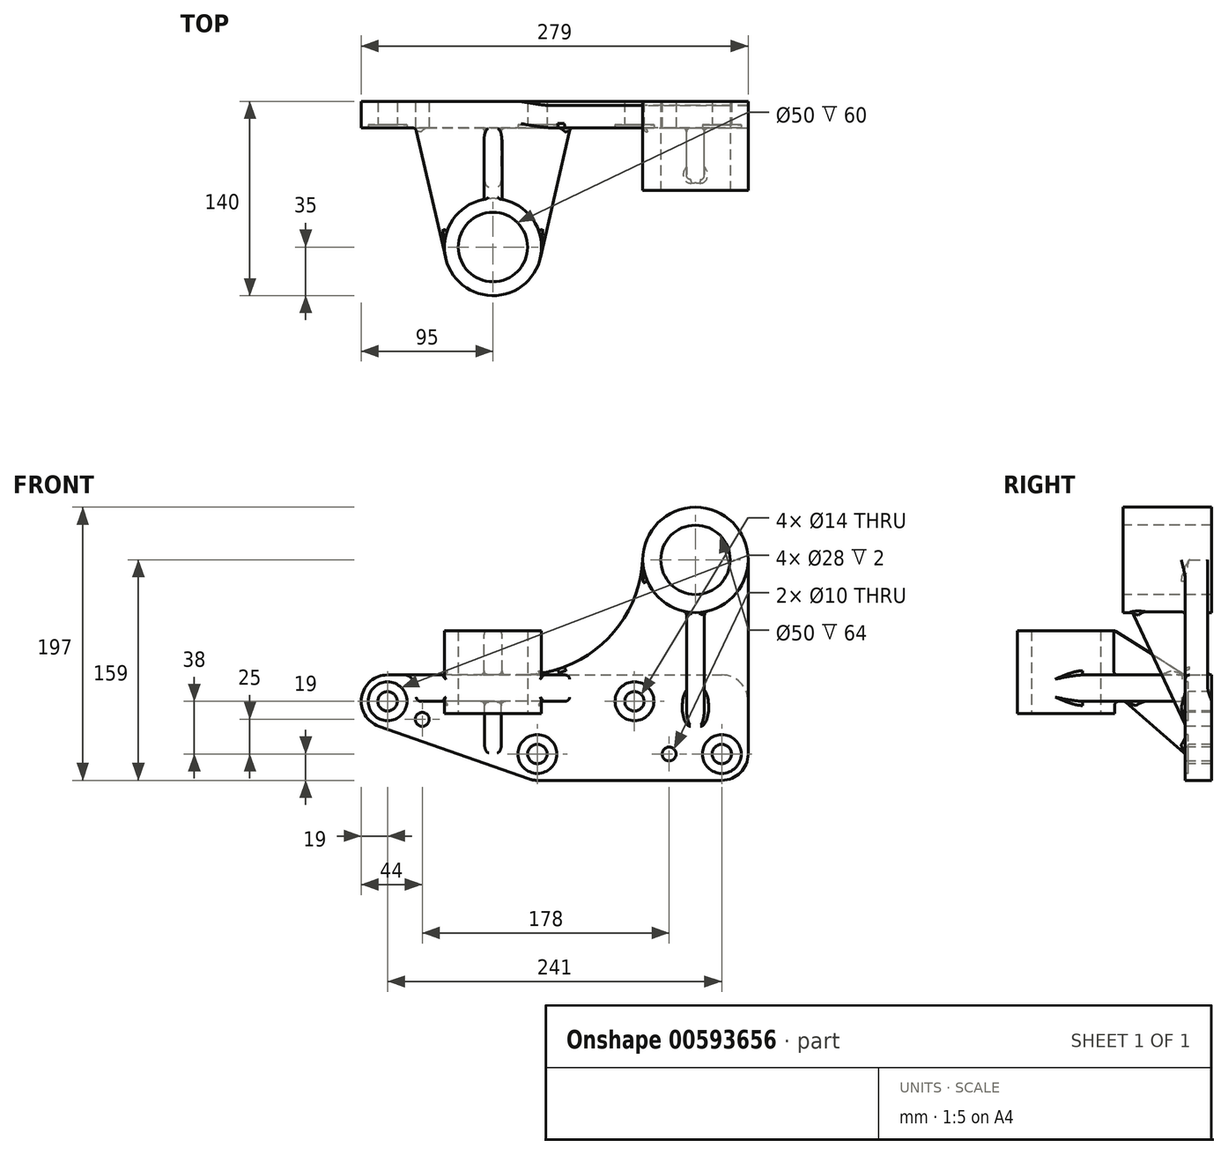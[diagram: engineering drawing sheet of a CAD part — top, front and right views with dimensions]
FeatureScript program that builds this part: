
annotation { "Feature Type Name" : "Feature", "Feature Type Description" : "" }
export const myFeature = defineFeature(function(context is Context, id is Id, definition is map)
    precondition{}
    {
        {
            var Q0;
            Q0=qCreatedBy(makeId("Front.planeOp"),FACE);
            var sketch = newSketch(context, id + "F0", { "sketchPlane" : qUnion([Q0])});
            skArc(sketch, "E0", {"start": v(0, -19) * mm, "mid": v(13.44, -13.44) * mm, "end": v(19, 0) * mm});
            skLineSegment(sketch, "E1", {"start": v(0, -19) * mm, "end": v(-133, -19) * mm});
            skLineSegment(sketch, "E2", {"start": v(-57.06, 140) * mm, "end": v(-57, 140) * mm, "construction": true});
            skArc(sketch, "E3", {"start": v(19, 140) * mm, "mid": v(-19, 178) * mm, "end": v(-57, 140) * mm});
            skLineSegment(sketch, "E4", {"start": v(19, 0) * mm, "end": v(19, 140) * mm});
            skLineSegment(sketch, "E5", {"start": v(-241, 57) * mm, "end": v(-144.86, 57) * mm});
            skArc(sketch, "E6", {"start": v(-241, 57) * mm, "mid": v(-259.73, 41.2) * mm, "end": v(-247.3, 20.08) * mm});
            skPoint(sketch, "E7", {"position": v(-133, 0) * mm});
            skLineSegment(sketch, "E8", {"start": v(-133, -19) * mm, "end": v(-133, 0) * mm, "construction": true});
            skArc(sketch, "E9", {"start": v(-139.3, -17.92) * mm, "mid": v(-136.2, -18.73) * mm, "end": v(-133, -19) * mm});
            skLineSegment(sketch, "E10", {"start": v(-247.3, 20.08) * mm, "end": v(-139.3, -17.92) * mm});
            skArc(sketch, "E11", {"start": v(-144.86, 57) * mm, "mid": v(-84.43, 81.03) * mm, "end": v(-57, 140) * mm});
            skSolve(sketch);
        }
        {
            var Q0;
            Q0 = qSketchRegion(id + "F0", true);
            extrude(context, id + "F1", {"entities" : qUnion([Q0]), "depth" : 19 * mm, "offsetDistance" : 25 * mm});
        }
        {
            var Q0;
            Q0=makeQuery(id+"F1.opExtrude","CAP_FACE",FACE,{"disambiguationData":[OSD([sQuery(id+"F0.wireOp",EDGE,"E0"),sQuery(id+"F0.wireOp",EDGE,"E1"),sQuery(id+"F0.wireOp",EDGE,"E3"),sQuery(id+"F0.wireOp",EDGE,"E4"),sQuery(id+"F0.wireOp",EDGE,"E5"),sQuery(id+"F0.wireOp",EDGE,"E6"),sQuery(id+"F0.wireOp",EDGE,"E9"),sQuery(id+"F0.wireOp",EDGE,"E10"),sQuery(id+"F0.wireOp",EDGE,"E11")])],"isStart":true});
            var sketch = newSketch(context, id + "F2", { "sketchPlane" : qUnion([Q0])});
            skCircle(sketch, "E12", {"center": v(19, 140) * mm, "radius": 38 * mm});
            skSolve(sketch);
        }
        {
            var Q0;
            Q0 = qSketchRegion(id + "F2", true);
            extrude(context, id + "F3", {"entities" : qUnion([Q0]), "operationType" : NewBodyOperationType.ADD, "oppositeDirection" : true, "depth" : 64 * mm, "offsetDistance" : 25 * mm});
        }
        {
            var Q0;
            Q0=makeQuery(id+"F1.opExtrude","SWEPT_FACE",FACE,{"disambiguationData":[OSD([sQuery(id+"F0.wireOp",EDGE,"E5")])]});
            var sketch = newSketch(context, id + "F4", { "sketchPlane" : qUnion([Q0])});
            skLineSegment(sketch, "E13", {"start": v(19, -64) * mm, "end": v(-57, -64) * mm});
            skPoint(sketch, "E14", {"position": v(-19, -64) * mm});
            skLineSegment(sketch, "E15", {"start": v(-165, -19) * mm, "end": v(-165, -105) * mm, "construction": true});
            skArc(sketch, "E16", {"start": v(-199.1, -112.87) * mm, "mid": v(-165, -140) * mm, "end": v(-130.9, -112.87) * mm});
            skLineSegment(sketch, "E17", {"start": v(-130.9, -112.87) * mm, "end": v(-109.22, -19) * mm});
            skLineSegment(sketch, "E18.MirrorCS", {"start": v(-199.1, -112.87) * mm, "end": v(-220.78, -19) * mm});
            skLineSegment(sketch, "E19", {"start": v(-109.22, -19) * mm, "end": v(-220.78, -19) * mm});
            skSolve(sketch);
        }
        {
            var Q0;
            Q0 = qSketchRegion(id + "F4", true);
            extrude(context, id + "F5", {"entities" : qUnion([Q0]), "operationType" : NewBodyOperationType.ADD, "oppositeDirection" : true, "depth" : 19 * mm, "offsetDistance" : 25 * mm});
        }
        {
            var Q0;
            Q0=makeQuery(id+"F5.boolean.opBoolean","MERGE",FACE,{"derivedFrom":[makeQuery(id+"F1.opExtrude","SWEPT_FACE",FACE,{"disambiguationData":[OSD([sQuery(id+"F0.wireOp",EDGE,"E5")])]}),makeQuery(id+"F5.opExtrude","CAP_FACE",FACE,{"disambiguationData":[OSD([sQuery(id+"F4.wireOp",EDGE,"E16"),sQuery(id+"F4.wireOp",EDGE,"E17"),sQuery(id+"F4.wireOp",EDGE,"E18.MirrorCS"),sQuery(id+"F4.wireOp",EDGE,"E19")])],"isStart":true})]});
            var sketch = newSketch(context, id + "F6", { "sketchPlane" : qUnion([Q0])});
            skCircle(sketch, "E20", {"center": v(-165, -105) * mm, "radius": 35 * mm});
            skSolve(sketch);
        }
        {
            var Q0;
            Q0 = qSketchRegion(id + "F6", true);
            extrude(context, id + "F7", {"entities" : qUnion([Q0]), "operationType" : NewBodyOperationType.ADD, "depth" : 32 * mm, "offsetDistance" : 25 * mm, "hasSecondDirection" : true, "secondDirectionOppositeDirection" : true, "secondDirectionDepth" : 28 * mm});
        }
        {
            var Q0;
            Q0=makeQuery(id+"F1.opExtrude","CAP_FACE",FACE,{"disambiguationData":[OSD([sQuery(id+"F0.wireOp",EDGE,"E0"),sQuery(id+"F0.wireOp",EDGE,"E1"),sQuery(id+"F0.wireOp",EDGE,"E3"),sQuery(id+"F0.wireOp",EDGE,"E4"),sQuery(id+"F0.wireOp",EDGE,"E5"),sQuery(id+"F0.wireOp",EDGE,"E6"),sQuery(id+"F0.wireOp",EDGE,"E9"),sQuery(id+"F0.wireOp",EDGE,"E10"),sQuery(id+"F0.wireOp",EDGE,"E11")])],"isStart":true});
            var sketch = newSketch(context, id + "F8", { "sketchPlane" : qUnion([Q0])});
            skLineSegment(sketch, "E21", {"start": v(-19, 38) * mm, "end": v(-19, 140) * mm});
            skArc(sketch, "E22.0", {"start": v(144.86, 57) * mm, "mid": v(84.43, 81.03) * mm, "end": v(57, 140) * mm});
            skArc(sketch, "E23", {"start": v(-19, 140) * mm, "mid": v(19, 102) * mm, "end": v(57, 140) * mm});
            skLineSegment(sketch, "E24", {"start": v(144.86, 57) * mm, "end": v(0, 57) * mm});
            skArc(sketch, "E25", {"start": v(0, 57) * mm, "mid": v(-13.44, 51.44) * mm, "end": v(-19, 38) * mm});
            skSolve(sketch);
        }
        {
            var Q0;
            Q0 = qSketchRegion(id + "F8", true);
            extrude(context, id + "F9", {"entities" : qUnion([Q0]), "operationType" : NewBodyOperationType.REMOVE, "oppositeDirection" : true, "depth" : 3 * mm, "offsetDistance" : 25 * mm});
        }
        {
            var Q0;
            Q0=makeQuery(id+"F9.boolean.opBoolean","MERGE",FACE,{"derivedFrom":[makeQuery(id+"F3.boolean.opBoolean","MERGE",FACE,{"derivedFrom":[makeQuery(id+"F1.opExtrude","SWEPT_FACE",FACE,{"disambiguationData":[OSD([sQuery(id+"F0.wireOp",EDGE,"E3")])]}),makeQuery(id+"F3.opExtrude","SWEPT_FACE",FACE,{"disambiguationData":[OSD([sQuery(id+"F2.wireOp",EDGE,"E12")])]})]}),makeQuery(id+"F9.opExtrude","SWEPT_FACE",FACE,{"disambiguationData":[OSD([sQuery(id+"F8.wireOp",EDGE,"E23")])]})]});
            cPlane(context, id + "F10", {"entities" : qUnion([Q0]), "cplaneType" : CPlaneType.LINE_ANGLE, "offset" : 25 * mm, "angle" : 90 * degree, "oppositeDirection" : true, "width" : 150 * mm, "height" : 150 * mm});
        }
        {
            var Q0;
            Q0=qCreatedBy(id+"F10.planeOp",FACE);
            var sketch = newSketch(context, id + "F11", { "sketchPlane" : qUnion([Q0])});
            skLineSegment(sketch, "E26.0", {"start": v(64, 178) * mm, "end": v(64, 102) * mm, "construction": true});
            skLineSegment(sketch, "E27.0", {"start": v(0, 178) * mm, "end": v(0, 102) * mm, "construction": true});
            skLineSegment(sketch, "E28", {"start": v(64, 178) * mm, "end": v(0, 178) * mm, "construction": true});
            skLineSegment(sketch, "E29", {"start": v(64, 102) * mm, "end": v(0, 102) * mm, "construction": true});
            skLineSegment(sketch, "E30", {"start": v(59.33, 107) * mm, "end": v(19, 107) * mm});
            skPoint(sketch, "E31", {"position": v(57, 102) * mm});
            skLineSegment(sketch, "E32", {"start": v(57, 102) * mm, "end": v(19, 20.5) * mm});
            skLineSegment(sketch, "E33", {"start": v(19, 20.5) * mm, "end": v(19, 107) * mm});
            skLineSegment(sketch, "E34", {"start": v(57, 102) * mm, "end": v(59.33, 107) * mm});
            skSolve(sketch);
        }
        {
            var Q0;
            Q0=makeQuery(id+"F11.imprint","IMPRINT",FACE,{"disambiguationData":[TD([[makeQuery(id+"F11.imprint","IMPRINT",EDGE,{"derivedFrom":sQuery(id+"F11.wireOp",EDGE,"E30")}),1.0]])]});
            extrude(context, id + "F12", {"entities" : qUnion([Q0]), "operationType" : NewBodyOperationType.ADD, "endBound" : BoundingType.SYMMETRIC, "depth" : 13 * mm, "offsetDistance" : 25 * mm});
        }
        {
            var Q0;
            Q0=makeQuery(id+"F7.boolean.opBoolean","MERGE",FACE,{"derivedFrom":[makeQuery(id+"F5.opExtrude","SWEPT_FACE",FACE,{"disambiguationData":[OSD([sQuery(id+"F4.wireOp",EDGE,"E16")])]}),makeQuery(id+"F7.opExtrude","SWEPT_FACE",FACE,{"disambiguationData":[OSD([sQuery(id+"F6.wireOp",EDGE,"E20")])]})]});
            cPlane(context, id + "F13", {"entities" : qUnion([Q0]), "cplaneType" : CPlaneType.LINE_ANGLE, "offset" : 25 * mm, "angle" : 0 * degree, "width" : 150 * mm, "height" : 150 * mm});
        }
        {
            var Q0;
            Q0=qCreatedBy(id+"F13.planeOp",FACE);
            var sketch = newSketch(context, id + "F14", { "sketchPlane" : qUnion([Q0])});
            skLineSegment(sketch, "E35.0", {"start": v(-140, 89) * mm, "end": v(-70, 89) * mm, "construction": true});
            skLineSegment(sketch, "E36.0", {"start": v(-140, 29) * mm, "end": v(-70, 29) * mm, "construction": true});
            skLineSegment(sketch, "E37", {"start": v(-70, 89) * mm, "end": v(-70, 29) * mm, "construction": true});
            skLineSegment(sketch, "E38", {"start": v(-75, 89) * mm, "end": v(-75, 57) * mm});
            skLineSegment(sketch, "E39", {"start": v(-75, 89) * mm, "end": v(-70, 89) * mm});
            skLineSegment(sketch, "E40", {"start": v(-70, 89) * mm, "end": v(-19, 57) * mm});
            skLineSegment(sketch, "E41", {"start": v(-19, 57) * mm, "end": v(-75, 57) * mm});
            skSolve(sketch);
        }
        {
            var Q0;
            Q0=makeQuery(id+"F14.imprint","IMPRINT",FACE,{"disambiguationData":[TD([[makeQuery(id+"F14.imprint","IMPRINT",EDGE,{"derivedFrom":sQuery(id+"F14.wireOp",EDGE,"E38")}),1.0]])]});
            extrude(context, id + "F15", {"entities" : qUnion([Q0]), "operationType" : NewBodyOperationType.ADD, "endBound" : BoundingType.SYMMETRIC, "depth" : 13 * mm, "offsetDistance" : 25 * mm});
        }
        {
            var Q0;
            Q0=qCreatedBy(id+"F13.planeOp",FACE);
            var sketch = newSketch(context, id + "F16", { "sketchPlane" : qUnion([Q0])});
            skLineSegment(sketch, "E42", {"start": v(-19, 0) * mm, "end": v(-19, 43) * mm});
            skLineSegment(sketch, "E43", {"start": v(-19, 43) * mm, "end": v(-68.47, 43) * mm});
            skLineSegment(sketch, "E44", {"start": v(-19, 0) * mm, "end": v(-68.47, 43) * mm});
            skSolve(sketch);
        }
        {
            var Q0;
            Q0=makeQuery(id+"F16.imprint","IMPRINT",FACE,{"disambiguationData":[TD([[makeQuery(id+"F16.imprint","IMPRINT",EDGE,{"derivedFrom":sQuery(id+"F16.wireOp",EDGE,"E42")}),1.0]])]});
            extrude(context, id + "F17", {"entities" : qUnion([Q0]), "operationType" : NewBodyOperationType.ADD, "endBound" : BoundingType.SYMMETRIC, "depth" : 12 * mm, "offsetDistance" : 25 * mm});
        }
        {
            var Q0;
            Q0=makeQuery(id+"F1.opExtrude","CAP_FACE",FACE,{"disambiguationData":[OSD([sQuery(id+"F0.wireOp",EDGE,"E0"),sQuery(id+"F0.wireOp",EDGE,"E1"),sQuery(id+"F0.wireOp",EDGE,"E3"),sQuery(id+"F0.wireOp",EDGE,"E4"),sQuery(id+"F0.wireOp",EDGE,"E5"),sQuery(id+"F0.wireOp",EDGE,"E6"),sQuery(id+"F0.wireOp",EDGE,"E9"),sQuery(id+"F0.wireOp",EDGE,"E10"),sQuery(id+"F0.wireOp",EDGE,"E11")])],"isStart":false});
            var sketch = newSketch(context, id + "F18", { "sketchPlane" : qUnion([Q0])});
            skPoint(sketch, "E45", {"position": v(-241, 38) * mm});
            skPoint(sketch, "E46", {"position": v(-216, 25) * mm});
            skPoint(sketch, "E47", {"position": v(-133, 0) * mm});
            skPoint(sketch, "E48", {"position": v(-38, 0) * mm});
            skPoint(sketch, "E49", {"position": v(-63, 38) * mm});
            skPoint(sketch, "E50", {"position": v(0, 0) * mm});
            skSolve(sketch);
        }
        {
            var Q0;
            Q0=makeQuery(id+"F7.opExtrude","CAP_FACE",FACE,{"disambiguationData":[OSD([sQuery(id+"F6.wireOp",EDGE,"E20")])],"isStart":true});
            var sketch = newSketch(context, id + "F19", { "sketchPlane" : qUnion([Q0])});
            skPoint(sketch, "E51", {"position": v(-165, 105) * mm});
            skSolve(sketch);
        }
        {
            var Q0;
            Q0=makeQuery(id+"F3.opExtrude","CAP_FACE",FACE,{"disambiguationData":[OSD([sQuery(id+"F2.wireOp",EDGE,"E12")])],"isStart":false});
            var sketch = newSketch(context, id + "F20", { "sketchPlane" : qUnion([Q0])});
            skPoint(sketch, "E52", {"position": v(-19, 140) * mm});
            skSolve(sketch);
        }
        {
            var Q0;
            Q0=sQuery(id+"F18.wireOp",VERTEX,"E46");
            var Q1;
            Q1=sQuery(id+"F18.wireOp",VERTEX,"E48");
            var Q2;
            Q2=makeQuery(id+"F1.opExtrude","SWEPT_BODY",BODY,{"disambiguationData":[OSD([sQuery(id+"F0.wireOp",EDGE,"E0"),sQuery(id+"F0.wireOp",EDGE,"E1"),sQuery(id+"F0.wireOp",EDGE,"E3"),sQuery(id+"F0.wireOp",EDGE,"E4"),sQuery(id+"F0.wireOp",EDGE,"E5"),sQuery(id+"F0.wireOp",EDGE,"E6"),sQuery(id+"F0.wireOp",EDGE,"E9"),sQuery(id+"F0.wireOp",EDGE,"E10"),sQuery(id+"F0.wireOp",EDGE,"E11")])]});
            hole(context, id + "F21", {"style" : HoleStyle.SIMPLE, "endStyle" : HoleEndStyle.THROUGH, "holeDiameter" : 10 * mm, "majorDiameter" : 6.35 * mm, "tappedDepth" : 12 * mm, "tapClearance" : 3, "startFromSketch" : true, "locations" : qUnion([Q0, Q1]), "scope" : qUnion([Q2])});
        }
        {
            var Q0;
            Q0=sQuery(id+"F18.wireOp",VERTEX,"E45");
            var Q1;
            Q1=sQuery(id+"F18.wireOp",VERTEX,"E47");
            var Q2;
            Q2=sQuery(id+"F18.wireOp",VERTEX,"E49");
            var Q3;
            Q3=sQuery(id+"F18.wireOp",VERTEX,"E50");
            var Q4;
            Q4=makeQuery(id+"F1.opExtrude","SWEPT_BODY",BODY,{"disambiguationData":[OSD([sQuery(id+"F0.wireOp",EDGE,"E0"),sQuery(id+"F0.wireOp",EDGE,"E1"),sQuery(id+"F0.wireOp",EDGE,"E3"),sQuery(id+"F0.wireOp",EDGE,"E4"),sQuery(id+"F0.wireOp",EDGE,"E5"),sQuery(id+"F0.wireOp",EDGE,"E6"),sQuery(id+"F0.wireOp",EDGE,"E9"),sQuery(id+"F0.wireOp",EDGE,"E10"),sQuery(id+"F0.wireOp",EDGE,"E11")])]});
            hole(context, id + "F22", {"style" : HoleStyle.C_BORE, "endStyle" : HoleEndStyle.THROUGH, "holeDiameter" : 14 * mm, "cBoreDiameter" : 28 * mm, "cBoreDepth" : 2 * mm, "majorDiameter" : 5 * mm, "tappedDepth" : 12 * mm, "tapClearance" : 3, "startFromSketch" : true, "locations" : qUnion([Q0, Q1, Q2, Q3]), "scope" : qUnion([Q4])});
        }
        {
            var Q0;
            Q0=sQuery(id+"F20.wireOp",VERTEX,"E52");
            var Q1;
            Q1=sQuery(id+"F19.wireOp",VERTEX,"E51");
            var Q2;
            Q2=makeQuery(id+"F1.opExtrude","SWEPT_BODY",BODY,{"disambiguationData":[OSD([sQuery(id+"F0.wireOp",EDGE,"E0"),sQuery(id+"F0.wireOp",EDGE,"E1"),sQuery(id+"F0.wireOp",EDGE,"E3"),sQuery(id+"F0.wireOp",EDGE,"E4"),sQuery(id+"F0.wireOp",EDGE,"E5"),sQuery(id+"F0.wireOp",EDGE,"E6"),sQuery(id+"F0.wireOp",EDGE,"E9"),sQuery(id+"F0.wireOp",EDGE,"E10"),sQuery(id+"F0.wireOp",EDGE,"E11")])]});
            hole(context, id + "F23", {"style" : HoleStyle.SIMPLE, "endStyle" : HoleEndStyle.THROUGH, "holeDiameter" : 50 * mm, "majorDiameter" : 5 * mm, "tappedDepth" : 12 * mm, "tapClearance" : 3, "locations" : qUnion([Q0, Q1]), "scope" : qUnion([Q2])});
        }
        {
            var Q0;
            Q0=makeQuery(id+"F17.opExtrude","SWEPT_FACE",FACE,{"disambiguationData":[OSD([sQuery(id+"F16.wireOp",EDGE,"E44")])]});
            var Q1;
            Q1=makeQuery(id+"F12.opExtrude","SWEPT_FACE",FACE,{"disambiguationData":[OSD([sQuery(id+"F11.wireOp",EDGE,"E32"),sQuery(id+"F11.wireOp",EDGE,"E34")])]});
            var Q2;
            Q2=makeQuery(id+"F5.opExtrude","SWEPT_FACE",FACE,{"disambiguationData":[OSD([sQuery(id+"F4.wireOp",EDGE,"E17")])]});
            var Q3;
            Q3=makeQuery(id+"F5.opExtrude","SWEPT_FACE",FACE,{"disambiguationData":[OSD([sQuery(id+"F4.wireOp",EDGE,"E18.MirrorCS")])]});
            var Q4;
            Q4=makeQuery(id+"F15.opExtrude","SWEPT_FACE",FACE,{"disambiguationData":[OSD([sQuery(id+"F14.wireOp",EDGE,"E40")])]});
            fillet(context, id + "F24", {"entities" : qUnion([Q0, Q1, Q2, Q3, Q4]), "radius" : 3 * mm, "tangentPropagation" : true, "allowEdgeOverflow" : false});
        }
        {
            var Q0;
            {var subQ0=makeQuery(id+"F3.opExtrude","SWEPT_FACE",FACE,{"disambiguationData":[OSD([sQuery(id+"F2.wireOp",EDGE,"E12")])]});var subQ1=sQuery(id+"F0.wireOp",EDGE,"E11");var subQ2=sQuery(id+"F0.wireOp",EDGE,"E3");var subQ3=makeQuery(id+"F1.opExtrude","CAP_FACE",FACE,{"disambiguationData":[OSD([sQuery(id+"F0.wireOp",EDGE,"E0"),sQuery(id+"F0.wireOp",EDGE,"E1"),subQ2,sQuery(id+"F0.wireOp",EDGE,"E4"),sQuery(id+"F0.wireOp",EDGE,"E5"),sQuery(id+"F0.wireOp",EDGE,"E6"),sQuery(id+"F0.wireOp",EDGE,"E9"),sQuery(id+"F0.wireOp",EDGE,"E10"),subQ1])],"isStart":false});Q0=makeQuery(id+"F12.boolean.opBoolean","SPLIT",EDGE,{"disambiguationData":[TD([makeQuery(id+"F1.opExtrude","SWEPT_FACE",FACE,{"disambiguationData":[OSD([subQ1])]})])],"derivedFrom":makeQuery(id+"F3.boolean.opBoolean","INTERSECT",EDGE,{"derivedFrom":[subQ3,subQ0]})});}
            var Q1;
            Q1=makeQuery(id+"F1.opExtrude","CAP_EDGE",EDGE,{"disambiguationData":[OSD([sQuery(id+"F0.wireOp",EDGE,"E11")])],"isStart":false});
            var Q2;
            Q2=makeQuery(id+"F9.boolean.opBoolean","COPY",EDGE,{"derivedFrom":makeQuery(id+"F9.opExtrude","CAP_EDGE",EDGE,{"disambiguationData":[OSD([sQuery(id+"F8.wireOp",EDGE,"E22.0")])],"isStart":false})});
            var Q3;
            {var subQ0=makeQuery(id+"F3.opExtrude","SWEPT_FACE",FACE,{"disambiguationData":[OSD([sQuery(id+"F2.wireOp",EDGE,"E12")])]});var subQ1=sQuery(id+"F0.wireOp",EDGE,"E4");var subQ2=sQuery(id+"F0.wireOp",EDGE,"E3");var subQ3=makeQuery(id+"F1.opExtrude","CAP_FACE",FACE,{"disambiguationData":[OSD([sQuery(id+"F0.wireOp",EDGE,"E0"),sQuery(id+"F0.wireOp",EDGE,"E1"),subQ2,subQ1,sQuery(id+"F0.wireOp",EDGE,"E5"),sQuery(id+"F0.wireOp",EDGE,"E6"),sQuery(id+"F0.wireOp",EDGE,"E9"),sQuery(id+"F0.wireOp",EDGE,"E10"),sQuery(id+"F0.wireOp",EDGE,"E11")])],"isStart":false});Q3=makeQuery(id+"F12.boolean.opBoolean","SPLIT",EDGE,{"disambiguationData":[TD([makeQuery(id+"F1.opExtrude","SWEPT_FACE",FACE,{"disambiguationData":[OSD([subQ1])]})])],"derivedFrom":makeQuery(id+"F3.boolean.opBoolean","INTERSECT",EDGE,{"derivedFrom":[subQ3,subQ0]})});}
            var Q4;
            Q4=makeQuery(id+"F7.boolean.opBoolean","INTERSECT",EDGE,{"derivedFrom":[makeQuery(id+"F5.opExtrude","CAP_FACE",FACE,{"disambiguationData":[OSD([sQuery(id+"F4.wireOp",EDGE,"E16"),sQuery(id+"F4.wireOp",EDGE,"E17"),sQuery(id+"F4.wireOp",EDGE,"E18.MirrorCS"),sQuery(id+"F4.wireOp",EDGE,"E19")])],"isStart":false}),makeQuery(id+"F7.opExtrude","SWEPT_FACE",FACE,{"disambiguationData":[OSD([sQuery(id+"F6.wireOp",EDGE,"E20")])]})]});
            fillet(context, id + "F25", {"entities" : qUnion([Q0, Q1, Q2, Q3, Q4]), "radius" : 3 * mm, "tangentPropagation" : true, "allowEdgeOverflow" : false});
        }
        {
            var Q0;
            {var subQ0=sQuery(id+"F4.wireOp",EDGE,"E18.MirrorCS");var subQ1=sQuery(id+"F4.wireOp",EDGE,"E16");var subQ2=makeQuery(id+"F5.opExtrude","CAP_FACE",FACE,{"disambiguationData":[OSD([subQ1,sQuery(id+"F4.wireOp",EDGE,"E17"),subQ0,sQuery(id+"F4.wireOp",EDGE,"E19")])],"isStart":true});var subQ3=makeQuery(id+"F1.opExtrude","SWEPT_FACE",FACE,{"disambiguationData":[OSD([sQuery(id+"F0.wireOp",EDGE,"E5")])]});var subQ4=makeQuery(id+"F7.opExtrude","SWEPT_FACE",FACE,{"disambiguationData":[OSD([sQuery(id+"F6.wireOp",EDGE,"E20")])]});Q0=makeQuery(id+"F15.boolean.opBoolean","SPLIT",EDGE,{"disambiguationData":[TD([makeQuery(id+"F5.opExtrude","SWEPT_FACE",FACE,{"disambiguationData":[OSD([subQ0])]})])],"derivedFrom":makeQuery(id+"F7.boolean.opBoolean","INTERSECT",EDGE,{"derivedFrom":[makeQuery(id+"F5.boolean.opBoolean","MERGE",FACE,{"derivedFrom":[subQ3,subQ2]}),subQ4]})});}
            var Q1;
            {var subQ0=sQuery(id+"F4.wireOp",EDGE,"E17");var subQ1=sQuery(id+"F4.wireOp",EDGE,"E16");var subQ2=makeQuery(id+"F5.opExtrude","CAP_FACE",FACE,{"disambiguationData":[OSD([subQ1,subQ0,sQuery(id+"F4.wireOp",EDGE,"E18.MirrorCS"),sQuery(id+"F4.wireOp",EDGE,"E19")])],"isStart":true});var subQ3=makeQuery(id+"F1.opExtrude","SWEPT_FACE",FACE,{"disambiguationData":[OSD([sQuery(id+"F0.wireOp",EDGE,"E5")])]});var subQ4=makeQuery(id+"F7.opExtrude","SWEPT_FACE",FACE,{"disambiguationData":[OSD([sQuery(id+"F6.wireOp",EDGE,"E20")])]});Q1=makeQuery(id+"F15.boolean.opBoolean","SPLIT",EDGE,{"disambiguationData":[TD([makeQuery(id+"F5.opExtrude","SWEPT_FACE",FACE,{"disambiguationData":[OSD([subQ0])]})])],"derivedFrom":makeQuery(id+"F7.boolean.opBoolean","INTERSECT",EDGE,{"derivedFrom":[makeQuery(id+"F5.boolean.opBoolean","MERGE",FACE,{"derivedFrom":[subQ3,subQ2]}),subQ4]})});}
            var Q2;
            Q2=makeQuery(id+"F9.boolean.opBoolean","COPY",EDGE,{"derivedFrom":makeQuery(id+"F9.opExtrude","CAP_EDGE",EDGE,{"disambiguationData":[OSD([sQuery(id+"F8.wireOp",EDGE,"E24")])],"isStart":false})});
            var Q3;
            Q3=makeQuery(id+"F9.boolean.opBoolean","COPY",EDGE,{"derivedFrom":makeQuery(id+"F9.opExtrude","CAP_EDGE",EDGE,{"disambiguationData":[OSD([sQuery(id+"F8.wireOp",EDGE,"E21")])],"isStart":false})});
            fillet(context, id + "F26", {"entities" : qUnion([Q0, Q1, Q2, Q3]), "radius" : 3 * mm, "tangentPropagation" : true, "allowEdgeOverflow" : false});
        }
    });
